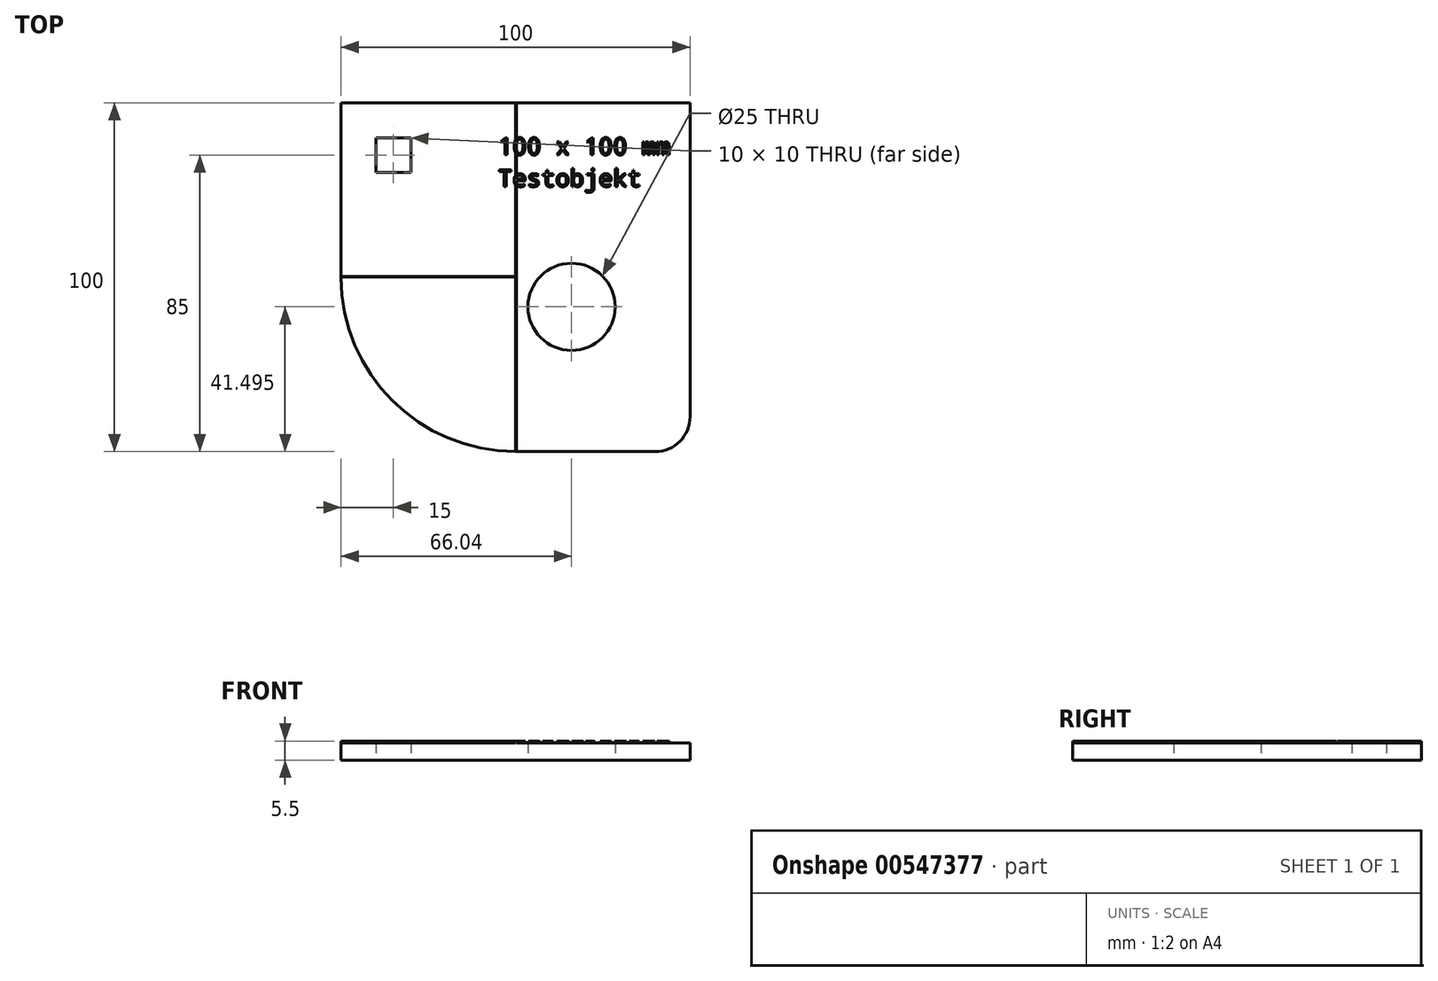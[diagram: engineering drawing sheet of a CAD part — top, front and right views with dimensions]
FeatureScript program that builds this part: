
annotation { "Feature Type Name" : "Feature", "Feature Type Description" : "" }
export const myFeature = defineFeature(function(context is Context, id is Id, definition is map)
    precondition{}
    {
        {
            var Q0;
            Q0=qCreatedBy(makeId("Top.planeOp"),FACE);
            var sketch = newSketch(context, id + "F0", { "sketchPlane" : qUnion([Q0])});
            skLineSegment(sketch, "E0.bottom", {"start": v(0, 0) * mm, "end": v(-100, 0) * mm});
            skLineSegment(sketch, "E0.top", {"start": v(0, 100) * mm, "end": v(-100, 100) * mm});
            skLineSegment(sketch, "E0.left", {"start": v(0, 0) * mm, "end": v(0, 100) * mm});
            skLineSegment(sketch, "E0.right", {"start": v(-100, 0) * mm, "end": v(-100, 100) * mm});
            skLineSegment(sketch, "E1.bottom", {"start": v(-90, 90) * mm, "end": v(-80, 90) * mm});
            skLineSegment(sketch, "E1.top", {"start": v(-90, 80) * mm, "end": v(-80, 80) * mm});
            skLineSegment(sketch, "E1.left", {"start": v(-90, 90) * mm, "end": v(-90, 80) * mm});
            skLineSegment(sketch, "E1.right", {"start": v(-80, 90) * mm, "end": v(-80, 80) * mm});
            skCircle(sketch, "E2", {"center": v(-33.96, 41.5) * mm, "radius": 12.5 * mm});
            skSolve(sketch);
        }
        {
            var Q0;
            Q0 = qSketchRegion(id + "F0", true);
            extrude(context, id + "F1", {"entities" : qUnion([Q0]), "depth" : 5 * mm, "offsetDistance" : 25 * mm});
        }
        {
            var Q0;
            Q0=makeQuery(id+"F1.opExtrude","SWEPT_EDGE",EDGE,{"disambiguationData":[OSD([sQuery(id+"F0.wireOp",EDGE,"E0.bottom"),sQuery(id+"F0.wireOp",EDGE,"E0.left")])]});
            fillet(context, id + "F2", {"entities" : qUnion([Q0]), "radius" : 10 * mm, "tangentPropagation" : true, "allowEdgeOverflow" : false});
        }
        {
            var Q0;
            Q0=makeQuery(id+"F1.opExtrude","SWEPT_EDGE",EDGE,{"disambiguationData":[OSD([sQuery(id+"F0.wireOp",EDGE,"E0.bottom"),sQuery(id+"F0.wireOp",EDGE,"E0.right")])]});
            fillet(context, id + "F3", {"entities" : qUnion([Q0]), "radius" : 50 * mm, "tangentPropagation" : true, "allowEdgeOverflow" : false});
        }
        {
            var Q0;
            Q0=makeQuery(id+"F1.opExtrude","CAP_FACE",FACE,{"disambiguationData":[OSD([sQuery(id+"F0.wireOp",EDGE,"E0.bottom"),sQuery(id+"F0.wireOp",EDGE,"E0.top"),sQuery(id+"F0.wireOp",EDGE,"E0.left"),sQuery(id+"F0.wireOp",EDGE,"E0.right"),sQuery(id+"F0.wireOp",EDGE,"E1.bottom"),sQuery(id+"F0.wireOp",EDGE,"E1.top"),sQuery(id+"F0.wireOp",EDGE,"E1.left"),sQuery(id+"F0.wireOp",EDGE,"E1.right"),sQuery(id+"F0.wireOp",EDGE,"E2")])],"isStart":false});
            var sketch = newSketch(context, id + "F4", { "sketchPlane" : qUnion([Q0])});
            skLineSegment(sketch, "E3", {"start": v(-50, 0) * mm, "end": v(-50, 100) * mm});
            skLineSegment(sketch, "E4", {"start": v(-50, 100) * mm, "end": v(-49.8, 100) * mm});
            skLineSegment(sketch, "E5", {"start": v(-49.8, 100) * mm, "end": v(-49.8, 0) * mm});
            skLineSegment(sketch, "E6", {"start": v(-49.8, 0) * mm, "end": v(-50, 0) * mm});
            skLineSegment(sketch, "E7.bottom", {"start": v(-100, 50) * mm, "end": v(-49.8, 50) * mm});
            skLineSegment(sketch, "E7.top", {"start": v(-100, 50.2) * mm, "end": v(-49.8, 50.2) * mm});
            skLineSegment(sketch, "E7.left", {"start": v(-100, 50) * mm, "end": v(-100, 50.2) * mm});
            skLineSegment(sketch, "E7.right", {"start": v(-49.8, 50) * mm, "end": v(-49.8, 50.2) * mm});
            skSolve(sketch);
        }
        {
            var Q0;
            Q0 = qSketchRegion(id + "F4", true);
            extrude(context, id + "F5", {"entities" : qUnion([Q0]), "operationType" : NewBodyOperationType.ADD, "depth" : 0.5 * mm, "offsetDistance" : 25 * mm});
        }
        {
            var Q0;
            {var subQ0=sQuery(id+"F0.wireOp",EDGE,"E1.top");var subQ1=sQuery(id+"F0.wireOp",EDGE,"E1.bottom");var subQ3=sQuery(id+"F0.wireOp",EDGE,"E0.right");var subQ4=sQuery(id+"F0.wireOp",EDGE,"E0.top");var subQ5=sQuery(id+"F0.wireOp",EDGE,"E1.left");var subQ6=sQuery(id+"F0.wireOp",EDGE,"E1.right");Q0=makeQuery(id+"F5.boolean.opBoolean","SPLIT",FACE,{"disambiguationData":[TD([makeQuery(id+"F1.opExtrude","SWEPT_FACE",FACE,{"disambiguationData":[OSD([subQ1])]})])],"derivedFrom":makeQuery(id+"F1.opExtrude","CAP_FACE",FACE,{"disambiguationData":[OSD([sQuery(id+"F0.wireOp",EDGE,"E0.bottom"),subQ4,sQuery(id+"F0.wireOp",EDGE,"E0.left"),subQ3,subQ1,subQ0,subQ5,subQ6,sQuery(id+"F0.wireOp",EDGE,"E2")])],"isStart":false})});}
            var sketch = newSketch(context, id + "F6", { "sketchPlane" : qUnion([Q0])});
            skText(sketch, "E8", { "text": "100 x 100 mm\nTestobjekt\n", "fontName": "DroidSansMono.ttf"});
            const initialGuessF6  = {"E8": [-0.055, 0.08507, 1, 0, 0.00493]};
            skSetInitialGuess(sketch, initialGuessF6);
            skSolve(sketch);
        }
        {
            var Q0;
            Q0 = qSketchRegion(id + "F6", true);
            extrude(context, id + "F7", {"entities" : qUnion([Q0]), "operationType" : NewBodyOperationType.ADD, "depth" : 0.5 * mm, "offsetDistance" : 25 * mm});
        }
    });
